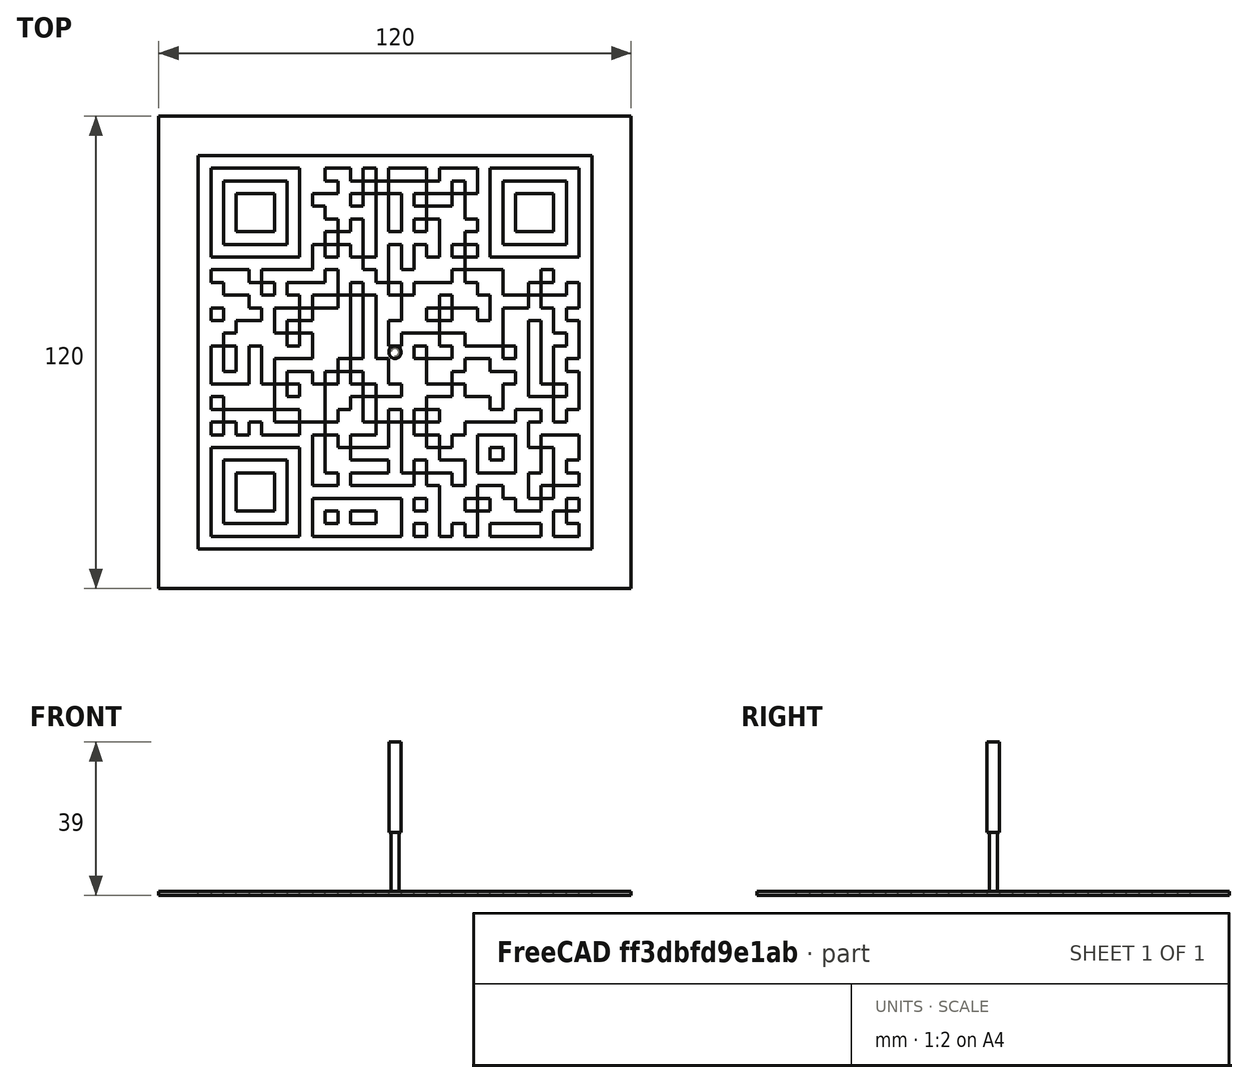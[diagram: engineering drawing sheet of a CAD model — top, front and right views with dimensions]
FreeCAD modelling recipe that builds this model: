
FCSTD DOCUMENT  (FreeCAD 1.0R)
Label: WechatQRCode
License: All rights reserved
objects: Part::Feature×4, Part::FeaturePython×4, Path::FeaturePython×4, Mesh::Feature×3, App::DocumentObjectGroup×3, App::FeaturePython×1, Sketcher::SketchObject×1, PartDesign::Pad×1, PartDesign::Body×1
note: 15 computed .brp shape members not serialized (recipe doc carries the construction recipe); baked Part::Feature solids carry a one-line shape summary decoded from their .brp

FEATURE [Mesh::Feature] ______________________1  label="教室门口展示牌_1"
FEATURE [Mesh::Feature] ______________________2  label="教室门口展示牌_2"
FEATURE [Part::Feature] ______________________003_solid  label="1 (Solid)"
  Placement = pos=(0,0,-1) rot=(0,0,1;0rad)
  shape: bbox 100 x 100 x 1 mm, 4116 faces (baked)
FEATURE [Part::Feature] ______________________003_solid001  label="2 (Solid)"
  Placement = pos=(0,0,-1) rot=(0,0,1;0rad)
  shape: bbox 93.55 x 93.55 x 1 mm, 3528 faces (baked)
FEATURE [App::FeaturePython] SetupSheet  # Path/CAM operation (typed FeaturePython)
  ClearanceHeightExpression = OpStockZMax+SetupSheet.ClearanceHeightOffset
  ClearanceHeightOffset = 5
  CoolantMode = 0
  CoolantModes = None | Flood | Mist
  FinalDepthExpression = OpFinalDepth
  HorizRapid = 0
  SafeHeightExpression = OpStockZMax+SetupSheet.SafeHeightOffset
  SafeHeightOffset = 3
  StartDepthExpression = OpStartDepth
  StepDownExpression = OpToolDiameter
  VertRapid = 0
FEATURE [Part::FeaturePython] Clone  label="Model-1 (Solid)"  # Draft clone (typed FeaturePython)
  AttacherType = Attacher::AttachEngine3D
  Fuse = false
  Objects = -> [______________________003_solid]
  PathResource = Model
  Placement = pos=(0,0,-1) rot=(0,0,1;0rad)
  Scale = (1,1,1)
FEATURE [App::DocumentObjectGroup] Model
  Group = -> [Clone]
FEATURE [Part::FeaturePython] Stock001  # WARN: FeaturePython — macro-defined, semantics opaque (R4)
  Height = 1
  Length = 100
  Placement = pos=(-50,-50,-1) rot=(0,0,1;0rad)
  StockType = CreateBox
  Width = 100
FEATURE [Part::FeaturePython] ToolBit001  label="1_5mm"  # Path/CAM toolbit (typed FeaturePython)
  BitPropertyNames = Chipload | CuttingEdgeHeight | Diameter | Flutes | Length | Material | ShankDiameter | SpindleDirection
  BitShape = <path>
  Chipload = 0
  CuttingEdgeHeight = 8
  Diameter = 1.5
  File = <userpath>/.local/share/FreeCAD/Macro/Bit/1.fctb
  Flutes = 0
  Length = 38
  Material = 0
  ShankDiameter = 3.17
  ShapeName = endmill
  SpindleDirection = 0
FEATURE [Path::FeaturePython] __5mm  label="1_5mm001"  # Path/CAM operation (typed FeaturePython)
  HorizFeed = 2
  HorizRapid = 0
  SpindleDir = 0
  SpindleSpeed = 10000
  Tool = -> ToolBit001
  ToolNumber = 2
  VertFeed = 2
  VertRapid = 0
  expr: HorizRapid = SetupSheet.HorizRapid
  expr: VertRapid = SetupSheet.VertRapid
FEATURE [Mesh::Feature] _____________________  label="教室门口展示牌"
FEATURE [Part::Feature] _____________________001
  shape: bbox 93.55 x 93.55 x 2e-07 mm, 876 faces, 0 solids (baked)
FEATURE [Part::Feature] _____________________001_solid  label="_____________________001 (Solid)"
  shape: bbox 93.55 x 93.55 x 2e-07 mm, 876 faces (baked)
FEATURE [Sketcher::SketchObject] Sketch
  ArcFitTolerance = 1e-06
  AttachmentSupport = -> [XY_Plane]
  FullyConstrained = true
  MakeInternals = false
  MapMode = 5
  sketch-geometry (5):
    g0: LineSegment StartX=-60 StartY=-60 StartZ=0 EndX=60 EndY=-60 EndZ=0
    g1: LineSegment StartX=60 StartY=-60 StartZ=0 EndX=60 EndY=60 EndZ=0
    g2: LineSegment StartX=60 StartY=60 StartZ=0 EndX=-60 EndY=60 EndZ=0
    g3: LineSegment StartX=-60 StartY=60 StartZ=0 EndX=-60 EndY=-60 EndZ=0
    g4: GeomPoint [constr] X=0 Y=0 Z=0
  constraints (12):
    c: Coincident(g0,g1)
    c: Coincident(g1,g2)
    c: Coincident(g2,g3)
    c: Coincident(g3,g0)
    c: Horizontal(g0)
    c: Horizontal(g2)
    c: Vertical(g1)
    c: Vertical(g3)
    c: Symmetric(g2,g0,g4)
    c: Distance(g1,g3) = 120
    c: Distance(g0,g2) = 120
    c: Coincident(g4,g-1)
FEATURE [PartDesign::Pad] Pad
  Direction = (0,0,1)
  Length = 1
  Length2 = 10
  Profile = -> Sketch
  ReferenceAxis = -> Sketch [N_Axis]
  Refine = true
  Suppressed = false
  Type = 0
FEATURE [PartDesign::Body] Body
  AllowCompound = false
  Group = -> [Sketch,Pad]
  Origin = -> Origin
  Placement = pos=(0,0,-1) rot=(0,0,1;0rad)
  Tip = -> Pad
FEATURE [Part::FeaturePython] ToolBit  label="2mm"  # Path/CAM toolbit (typed FeaturePython)
  BitPropertyNames = Chipload | CuttingEdgeHeight | Diameter | Flutes | Length | Material | ShankDiameter | SpindleDirection
  BitShape = <path>
  Chipload = 0
  CuttingEdgeHeight = 15
  Diameter = 2
  File = <userpath>/.local/share/FreeCAD/Macro/Bit/2mm.fctb
  Flutes = 0
  Length = 38
  Material = 0
  ShankDiameter = 3.17
  ShapeName = endmill
  SpindleDirection = 0
FEATURE [Path::FeaturePython] _mm  label="2mm001"  # Path/CAM operation (typed FeaturePython)
  HorizFeed = 5
  HorizRapid = 0
  SpindleDir = 0
  SpindleSpeed = 10000
  Tool = -> ToolBit
  ToolNumber = 3
  VertFeed = 5
  VertRapid = 0
  expr: HorizRapid = SetupSheet.HorizRapid
  expr: VertRapid = SetupSheet.VertRapid
FEATURE [App::DocumentObjectGroup] Tools
  Group = -> [__5mm,_mm]
FEATURE [Path::FeaturePython] Pocket_Shape  # Path/CAM operation (typed FeaturePython)
  Active = true
  AreaParams:
    Tolerance = 1e-07
    FitArcs = True
    Simplify = False
    CleanDistance = 0.0
    Accuracy = 0.01
    Unit = 1.0
    MinArcPoints = 4
    MaxArcPoints = 100
    ClipperScale = 10000000.0
    Fill = 0
    Coplanar = 0
    Reorient = True
    Outline = False
    Explode = False
    OpenMode = 0
    Deflection = 0.01
    SubjectFill = 0
    ClipFill = 0
    Offset = 0.0
    ExtraPass = 0
    Stepover = 0.0
    LastStepover = 0.0
    JoinType = 0
    EndType = 0
    MiterLimit = 2.0
    RoundPrecision = 0.0
    PocketMode = 4
    ToolRadius = 1.0
    PocketExtraOffset = 0.0
    PocketStepover = 2.0
    PocketLastStepover = 0.0
    FromCenter = True
    Angle = 45.0
    AngleShift = 0.0
    Shift = 0.0
    Thicken = False
    SectionCount = -1
    Stepdown = 1.0
    SectionOffset = 0.0
    SectionTolerance = 1e-06
    SectionMode = 2
    Project = False
  Base = -> [Clone]
  ClearanceHeight = 5
  CoolantMode = 0
  CutMode = 0
  CycleTime = 00:28:26
  ExtensionCorners = true
  ExtensionLengthDefault = 1
  ExtraOffset = 0
  FinalDepth = -1
  FinishDepth = 0
  KeepToolDown = false
  MinTravel = true
  OffsetPattern = 2
  OpFinalDepth = -1
  OpStartDepth = 0
  OpStockZMax = 0
  OpStockZMin = -1
  OpToolDiameter = 2
  PathParams = {'orientation': 1, 'sort_mode': 3, 'threshold': 2.0, 'feedrate': 5.0, 'feedrate_v': 5.0, 'verbose': True, 'resume_height': 3.0, 'retraction': 5.0, 'return_end': True, 'preamble': False, 'start': Vector (-41.322589999025816, -3.8387121176367884, 5.0)}
  PocketLastStepOver = 0
  SafeHeight = 3
  SplitArcs = false
  StartAt = 0
  StartDepth = 0
  StartPoint = (0,0,0)
  StepDown = 1
  StepOver = 100
  ToolController = -> _mm
  UseOutline = false
  UseRestMachining = false
  UseStartPoint = true
  ZigZagAngle = 45
  expr: ClearanceHeight = OpStockZMax + SetupSheet.ClearanceHeightOffset
  expr: ExtensionLengthDefault = OpToolDiameter / 2
  expr: FinalDepth = OpFinalDepth
  expr: SafeHeight = OpStockZMax + SetupSheet.SafeHeightOffset
  expr: StartDepth = OpStartDepth
  expr: StepDown = 1
FEATURE [App::DocumentObjectGroup] Operations
  Group = -> [Pocket_Shape]
FEATURE [Path::FeaturePython] Job  label="Job_1"  # Path/CAM operation (typed FeaturePython)
  CycleTime = 00:28:26
  Fixtures = G54
  GeometryTolerance = 0.01
  JobType = 0
  Model = -> Model
  Operations = -> Operations
  OrderOutputBy = 0
  PostProcessor = 11
  PostProcessorOutputFile = %DCode1.nc
  SetupSheet = -> SetupSheet
  SplitOutput = false
  Stock = -> Stock001
  Tools = -> Tools
note: 2 file-system paths scrubbed to <path> (originals preserved in the JSON sidecar)
